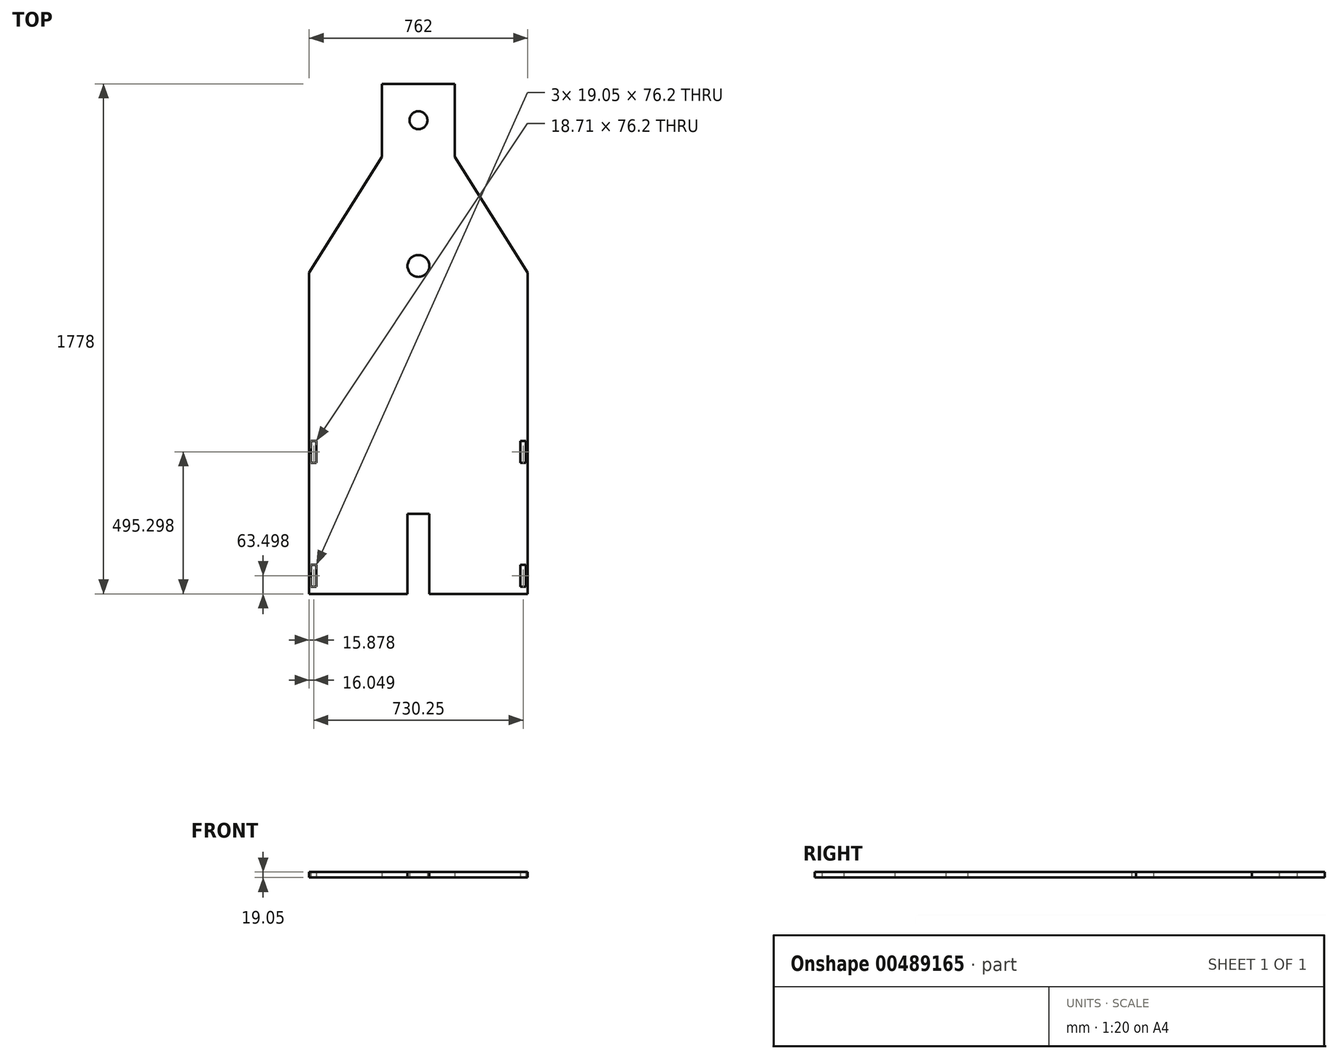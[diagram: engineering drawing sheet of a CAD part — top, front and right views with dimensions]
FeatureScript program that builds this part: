
annotation { "Feature Type Name" : "Feature", "Feature Type Description" : "" }
export const myFeature = defineFeature(function(context is Context, id is Id, definition is map)
    precondition{}
    {
        {
            var Q0;
            Q0=qCreatedBy(makeId("Top.planeOp"),FACE);
            var sketch = newSketch(context, id + "F0", { "sketchPlane" : qUnion([Q0])});
            skLineSegment(sketch, "E0.left", {"start": v(-844.69, -808.38) * mm, "end": v(-844.69, -833.78) * mm});
            skLineSegment(sketch, "E0.right", {"start": v(-82.69, 286.4) * mm, "end": v(-82.69, -833.78) * mm});
            skLineSegment(sketch, "E1.top", {"start": v(-336.69, 944.22) * mm, "end": v(-590.69, 944.22) * mm});
            skLineSegment(sketch, "E1.left", {"start": v(-336.69, 690.22) * mm, "end": v(-336.69, 944.22) * mm});
            skLineSegment(sketch, "E1.right", {"start": v(-590.69, 690.22) * mm, "end": v(-590.69, 944.22) * mm});
            skLineSegment(sketch, "E2.bottom", {"start": v(-838, -300.38) * mm, "end": v(-819.29, -300.38) * mm});
            skLineSegment(sketch, "E2.top", {"start": v(-838, -376.58) * mm, "end": v(-819.29, -376.58) * mm});
            skLineSegment(sketch, "E2.left", {"start": v(-819.29, -300.38) * mm, "end": v(-819.29, -376.58) * mm});
            skLineSegment(sketch, "E2.right", {"start": v(-838, -300.38) * mm, "end": v(-838, -376.58) * mm});
            skLineSegment(sketch, "E3.left", {"start": v(-838.34, -732.18) * mm, "end": v(-838.34, -808.38) * mm});
            skLineSegment(sketch, "E4.bottom", {"start": v(-838.34, -732.18) * mm, "end": v(-819.29, -732.18) * mm});
            skLineSegment(sketch, "E4.top", {"start": v(-838.34, -808.38) * mm, "end": v(-819.29, -808.38) * mm});
            skLineSegment(sketch, "E4.left", {"start": v(-819.29, -732.18) * mm, "end": v(-819.29, -808.38) * mm});
            skLineSegment(sketch, "E5.bottom", {"start": v(-108.09, -732.18) * mm, "end": v(-89.04, -732.18) * mm});
            skLineSegment(sketch, "E5.top", {"start": v(-108.09, -808.38) * mm, "end": v(-89.04, -808.38) * mm});
            skLineSegment(sketch, "E5.left", {"start": v(-89.04, -732.18) * mm, "end": v(-89.04, -808.38) * mm});
            skLineSegment(sketch, "E5.right", {"start": v(-108.09, -732.18) * mm, "end": v(-108.09, -808.38) * mm});
            skLineSegment(sketch, "E6.left", {"start": v(-88.7, -744.02) * mm, "end": v(-89.04, -808.38) * mm});
            skLineSegment(sketch, "E6.right", {"start": v(-107.75, -744.02) * mm, "end": v(-108.09, -808.38) * mm});
            skLineSegment(sketch, "E7.right", {"start": v(-88.7, -300.38) * mm, "end": v(-88.7, -376.58) * mm});
            skLineSegment(sketch, "E8.bottom", {"start": v(-107.75, -300.38) * mm, "end": v(-88.7, -300.38) * mm});
            skLineSegment(sketch, "E8.top", {"start": v(-107.75, -376.58) * mm, "end": v(-88.7, -376.58) * mm});
            skLineSegment(sketch, "E8.right", {"start": v(-107.75, -300.38) * mm, "end": v(-107.75, -376.58) * mm});
            skCircle(sketch, "E9", {"center": v(-463.69, 817.22) * mm, "radius": 31.3 * mm});
            skPoint(sketch, "E9.centerSnap0", {"position": v(-463.69, 944.22) * mm});
            skPoint(sketch, "E9.centerSnap1", {"position": v(-590.69, 817.22) * mm});
            skCircle(sketch, "E10", {"center": v(-463.69, 309.22) * mm, "radius": 38.1 * mm});
            skPoint(sketch, "E11.oppositeSnap0", {"position": v(-463.69, -833.78) * mm});
            skLineSegment(sketch, "E12", {"start": v(-107.75, -376.58) * mm, "end": v(-82.69, -376.58) * mm, "construction": true});
            skLineSegment(sketch, "E13", {"start": v(-82.69, -376.58) * mm, "end": v(-107.75, -376.58) * mm, "construction": true});
            skLineSegment(sketch, "E14", {"start": v(-108.09, -877.3) * mm, "end": v(-82.69, -877.3) * mm, "construction": true});
            skLineSegment(sketch, "E15", {"start": v(-838.34, -732.18) * mm, "end": v(-838, -376.58) * mm, "construction": true});
            skLineSegment(sketch, "E16", {"start": v(-819.29, -808.38) * mm, "end": v(-844.69, -808.38) * mm, "construction": true});
            skLineSegment(sketch, "E17", {"start": v(-844.69, -808.38) * mm, "end": v(-844.69, -376.58) * mm, "construction": true});
            skLineSegment(sketch, "E18", {"start": v(-844.69, -376.58) * mm, "end": v(-819.29, -376.58) * mm, "construction": true});
            skLineSegment(sketch, "E19", {"start": v(-336.69, 841.98) * mm, "end": v(-590.69, 841.98) * mm, "construction": true});
            skLineSegment(sketch, "E20", {"start": v(-82.69, -833.78) * mm, "end": v(-425.59, -833.78) * mm});
            skLineSegment(sketch, "E21.bottom", {"start": v(-501.79, -554.38) * mm, "end": v(-425.59, -554.38) * mm, "construction": true});
            skLineSegment(sketch, "E21.left", {"start": v(-501.79, -554.38) * mm, "end": v(-501.79, -833.78) * mm, "construction": true});
            skLineSegment(sketch, "E21.right", {"start": v(-425.59, -554.38) * mm, "end": v(-425.59, -833.78) * mm, "construction": true});
            skLineSegment(sketch, "E22", {"start": v(-425.59, -833.78) * mm, "end": v(-425.59, -554.38) * mm});
            skLineSegment(sketch, "E23", {"start": v(-501.79, -554.38) * mm, "end": v(-501.79, -833.78) * mm});
            skLineSegment(sketch, "E24.trimOffspring", {"start": v(-501.79, -833.78) * mm, "end": v(-844.69, -833.78) * mm});
            skPoint(sketch, "E21.top.start.orphan", {"position": v(-501.79, -1113.18) * mm});
            skPoint(sketch, "E25.orphan", {"position": v(-425.59, -1113.18) * mm});
            skLineSegment(sketch, "E26", {"start": v(-425.59, -554.38) * mm, "end": v(-501.79, -554.38) * mm});
            skLineSegment(sketch, "E27", {"start": v(-107.75, -376.58) * mm, "end": v(-108.09, -732.18) * mm, "construction": true});
            skLineSegment(sketch, "E28", {"start": v(-88.7, -300.38) * mm, "end": v(-838, -300.38) * mm, "construction": true});
            skLineSegment(sketch, "E29", {"start": v(-89.04, -732.18) * mm, "end": v(-88.7, -376.58) * mm, "construction": true});
            skLineSegment(sketch, "E30", {"start": v(-819.29, -732.18) * mm, "end": v(-819.29, -376.58) * mm, "construction": true});
            skLineSegment(sketch, "E31", {"start": v(-838.34, -808.38) * mm, "end": v(-89.04, -808.38) * mm, "construction": true});
            skLineSegment(sketch, "E32", {"start": v(-684.76, 0) * mm, "end": v(-684.76, -191.81) * mm, "construction": true});
            skLineSegment(sketch, "E33", {"start": v(-684.76, -191.81) * mm, "end": v(-291.79, -191.81) * mm, "construction": true});
            skLineSegment(sketch, "E34", {"start": v(-291.79, -191.81) * mm, "end": v(-291.79, 0) * mm, "construction": true});
            skLineSegment(sketch, "E35", {"start": v(-291.79, 0) * mm, "end": v(-684.76, 0) * mm, "construction": true});
            skLineSegment(sketch, "E36", {"start": v(-336.69, 690.22) * mm, "end": v(-82.69, 286.4) * mm});
            skLineSegment(sketch, "E37", {"start": v(-433.17, 286.4) * mm, "end": v(-494.2, 286.4) * mm});
            skLineSegment(sketch, "E38", {"start": v(-844.69, 286.4) * mm, "end": v(-590.69, 690.22) * mm});
            skLineSegment(sketch, "E39", {"start": v(-844.69, 286.4) * mm, "end": v(-838, -300.38) * mm});
            skLineSegment(sketch, "E40", {"start": v(-590.69, 944.22) * mm, "end": v(-590.69, 817.22) * mm});
            skLineSegment(sketch, "E41", {"start": v(-82.69, 286.4) * mm, "end": v(-326.2, 673.55) * mm});
            skLineSegment(sketch, "E42", {"start": v(-590.69, 944.22) * mm, "end": v(-590.69, 690.22) * mm});
            skLineSegment(sketch, "E43", {"start": v(-590.69, 944.22) * mm, "end": v(-336.69, 944.22) * mm});
            skLineSegment(sketch, "E44", {"start": v(-844.69, -833.78) * mm, "end": v(-844.69, 286.4) * mm});
            skLineSegment(sketch, "E45", {"start": v(-501.79, -542.3) * mm, "end": v(-425.59, -542.3) * mm});
            skLineSegment(sketch, "E46", {"start": v(-425.59, -542.3) * mm, "end": v(-425.59, -833.78) * mm});
            skLineSegment(sketch, "E47", {"start": v(-501.79, -833.78) * mm, "end": v(-425.59, -833.78) * mm});
            skSolve(sketch);
        }
        {
            var Q0;
            {var subQ5=sQuery(id+"F0.wireOp",EDGE,"E0.right");Q0=makeQuery(id+"F0.imprint","IMPRINT",FACE,{"disambiguationData":[TD([[makeQuery(id+"F0.imprint","IMPRINT",EDGE,{"derivedFrom":subQ5}),-1.0]])]});}
            var Q1;
            {var subQ2=sQuery(id+"F0.wireOp",EDGE,"E45");Q1=makeQuery(id+"F0.imprint","IMPRINT",FACE,{"disambiguationData":[TD([[makeQuery(id+"F0.imprint","IMPRINT",EDGE,{"derivedFrom":subQ2}),-1.0]])]});}
            extrude(context, id + "F1", {"entities" : qUnion([Q0, Q1]), "depth" : 19.05 * mm, "offsetDistance" : 25.4 * mm});
        }
    });
